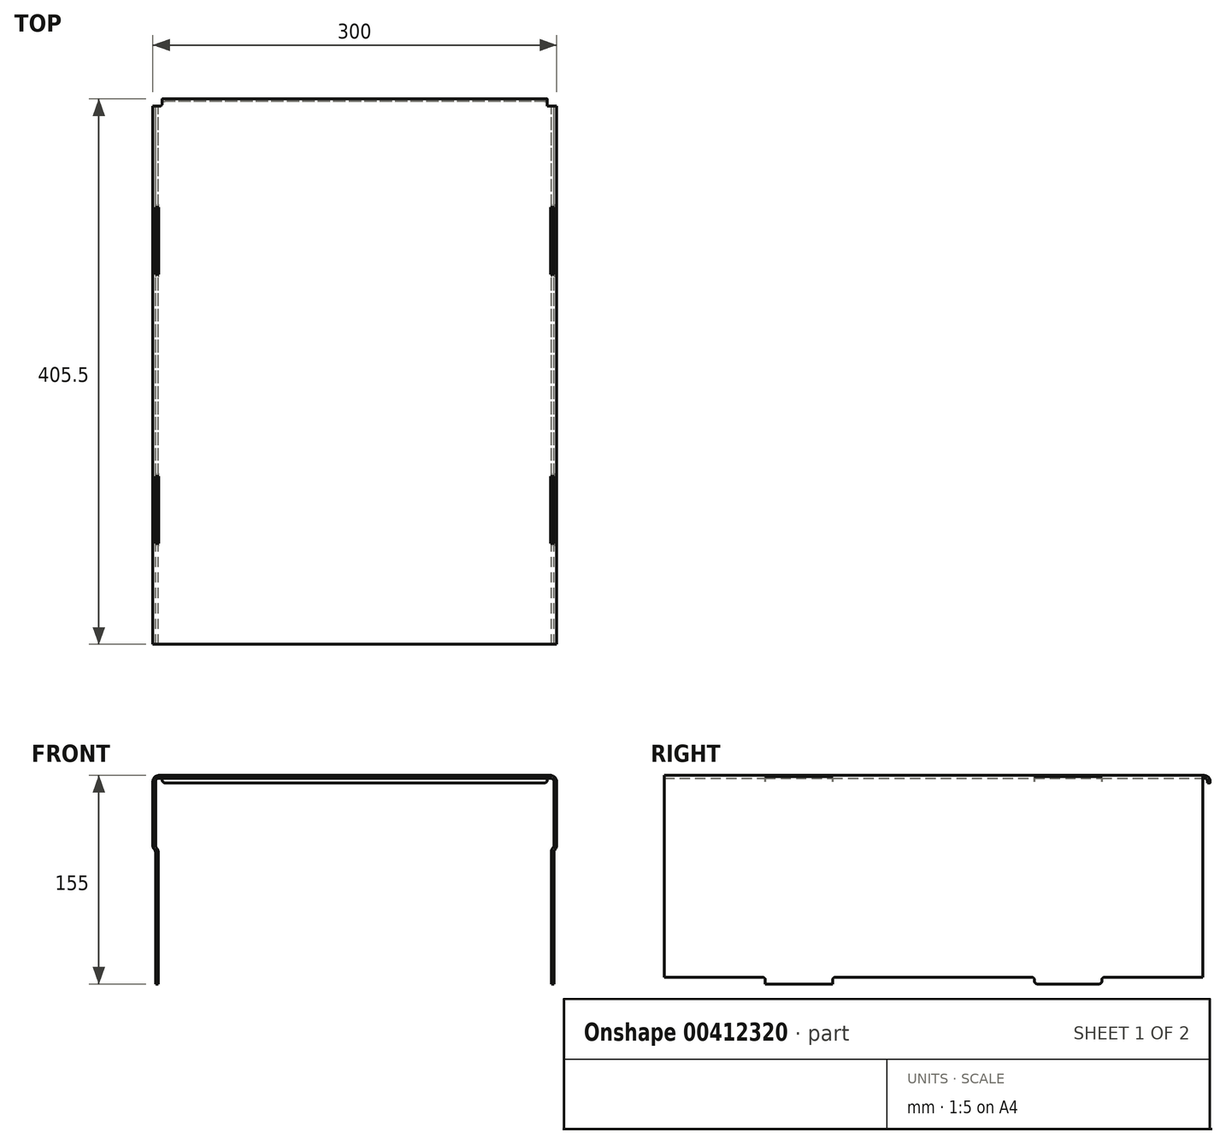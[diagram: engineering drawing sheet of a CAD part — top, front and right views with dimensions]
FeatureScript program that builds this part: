
annotation { "Feature Type Name" : "Feature", "Feature Type Description" : "" }
export const myFeature = defineFeature(function(context is Context, id is Id, definition is map)
    precondition{}
    {
        {
            var Q0;
            Q0=qCreatedBy(makeId("Front.planeOp"),FACE);
            var sketch = newSketch(context, id + "F0", { "sketchPlane" : qUnion([Q0])});
            skLineSegment(sketch, "E0.bottom", {"start": v(145.5, 77.5) * mm, "end": v(0, 77.5) * mm});
            skLineSegment(sketch, "E0.top", {"start": v(148, -77.5) * mm, "end": v(146, -77.5) * mm});
            skLineSegment(sketch, "E0.left", {"start": v(150, 73) * mm, "end": v(150, 25.5) * mm});
            skPoint(sketch, "E0.middle", {"position": v(0, 0) * mm});
            skLineSegment(sketch, "E1", {"start": v(148.95, 22.6) * mm, "end": v(148.58, 22.18) * mm});
            skLineSegment(sketch, "E2", {"start": v(148, 20.57) * mm, "end": v(148, -77.5) * mm});
            skPoint(sketch, "E3.visualSharp", {"position": v(150, 77.5) * mm});
            skArc(sketch, "E3.filletArc", {"start": v(150, 73) * mm, "mid": v(148.68, 76.18) * mm, "end": v(145.5, 77.5) * mm});
            skLineSegment(sketch, "E4", {"start": v(0, 75.5) * mm, "end": v(145.5, 75.5) * mm});
            skLineSegment(sketch, "E5.trimOffspring", {"start": v(148, 73) * mm, "end": v(148, 25.5) * mm});
            skPoint(sketch, "E6.visualSharp", {"position": v(148, 75.5) * mm});
            skArc(sketch, "E6.filletArc", {"start": v(148, 73) * mm, "mid": v(147.27, 74.77) * mm, "end": v(145.5, 75.5) * mm});
            skLineSegment(sketch, "E7", {"start": v(147.42, 23.9) * mm, "end": v(147.05, 23.46) * mm});
            skLineSegment(sketch, "E8", {"start": v(146, 20.57) * mm, "end": v(146, -77.5) * mm});
            skPoint(sketch, "E9.orphan", {"position": v(150, -77.5) * mm});
            skPoint(sketch, "E10.visualSharp", {"position": v(150, 23.86) * mm});
            skArc(sketch, "E10.filletArc", {"start": v(148.95, 22.6) * mm, "mid": v(149.73, 23.96) * mm, "end": v(150, 25.5) * mm});
            skPoint(sketch, "E11.visualSharp", {"position": v(148, 21.48) * mm});
            skArc(sketch, "E11.filletArc", {"start": v(148.58, 22.18) * mm, "mid": v(148.15, 21.42) * mm, "end": v(148, 20.57) * mm});
            skPoint(sketch, "E12.visualSharp", {"position": v(148, 24.6) * mm});
            skArc(sketch, "E12.filletArc", {"start": v(147.42, 23.9) * mm, "mid": v(147.85, 24.64) * mm, "end": v(148, 25.5) * mm});
            skPoint(sketch, "E13.visualSharp", {"position": v(146, 22.2) * mm});
            skArc(sketch, "E13.filletArc", {"start": v(147.05, 23.46) * mm, "mid": v(146.27, 22.1) * mm, "end": v(146, 20.57) * mm});
            skLineSegment(sketch, "E14", {"start": v(0, 0) * mm, "end": v(0, 158.87) * mm, "construction": true});
            skPoint(sketch, "E0.right.start.orphan", {"position": v(-150, 77.5) * mm});
            skLineSegment(sketch, "E15.MirrorCS", {"start": v(-145.5, 77.5) * mm, "end": v(0, 77.5) * mm});
            skLineSegment(sketch, "E16.MirrorCS", {"start": v(0, 75.5) * mm, "end": v(-145.5, 75.5) * mm});
            skArc(sketch, "E17.MirrorCS", {"start": v(-148, 73) * mm, "mid": v(-147.27, 74.77) * mm, "end": v(-145.5, 75.5) * mm});
            skArc(sketch, "E18.MirrorCS", {"start": v(-150, 73) * mm, "mid": v(-148.68, 76.18) * mm, "end": v(-145.5, 77.5) * mm});
            skLineSegment(sketch, "E19.MirrorCS", {"start": v(-148, 73) * mm, "end": v(-148, 25.5) * mm});
            skLineSegment(sketch, "E20.MirrorCS", {"start": v(-150, 73) * mm, "end": v(-150, 25.5) * mm});
            skLineSegment(sketch, "E21.MirrorCS", {"start": v(-148, 20.57) * mm, "end": v(-148, -77.5) * mm});
            skLineSegment(sketch, "E22.MirrorCS", {"start": v(-146, 20.57) * mm, "end": v(-146, -77.5) * mm});
            skArc(sketch, "E23.MirrorCS", {"start": v(-147.05, 23.46) * mm, "mid": v(-146.27, 22.1) * mm, "end": v(-146, 20.57) * mm});
            skArc(sketch, "E24.MirrorCS", {"start": v(-148.58, 22.18) * mm, "mid": v(-148.15, 21.42) * mm, "end": v(-148, 20.57) * mm});
            skArc(sketch, "E25.MirrorCS", {"start": v(-147.42, 23.9) * mm, "mid": v(-147.85, 24.64) * mm, "end": v(-148, 25.5) * mm});
            skArc(sketch, "E26.MirrorCS", {"start": v(-148.95, 22.6) * mm, "mid": v(-149.73, 23.96) * mm, "end": v(-150, 25.5) * mm});
            skLineSegment(sketch, "E27", {"start": v(-147.42, 23.9) * mm, "end": v(-147.05, 23.46) * mm});
            skLineSegment(sketch, "E28", {"start": v(-148.95, 22.6) * mm, "end": v(-148.58, 22.18) * mm});
            skLineSegment(sketch, "E29.trimOffspring", {"start": v(-146, -77.5) * mm, "end": v(-150, -77.5) * mm});
            skSolve(sketch);
        }
        {
            var Q0;
            Q0 = qSketchRegion(id + "F0", true);
            extrude(context, id + "F1", {"entities" : qUnion([Q0]), "depth" : 400 * mm});
        }
        {
            var Q0;
            Q0=makeQuery(id+"F1.opExtrude","SWEPT_FACE",FACE,{"disambiguationData":[OSD([sQuery(id+"F0.wireOp",EDGE,"E2")])]});
            var sketch = newSketch(context, id + "F2", { "sketchPlane" : qUnion([Q0])});
            skLineSegment(sketch, "E30", {"start": v(-430.94, -72.5) * mm, "end": v(45.78, -72.5) * mm});
            skLineSegment(sketch, "E31.bottom", {"start": v(-400, -77.5) * mm, "end": v(-325, -77.5) * mm});
            skLineSegment(sketch, "E31.top", {"start": v(-400, -72.5) * mm, "end": v(-325, -72.5) * mm});
            skLineSegment(sketch, "E31.left", {"start": v(-400, -77.5) * mm, "end": v(-400, -72.5) * mm});
            skLineSegment(sketch, "E31.right", {"start": v(-325, -77.5) * mm, "end": v(-325, -72.5) * mm});
            skLineSegment(sketch, "E32.bottom", {"start": v(0, -77.5) * mm, "end": v(-75, -77.5) * mm});
            skLineSegment(sketch, "E32.top", {"start": v(0, -72.5) * mm, "end": v(-75, -72.5) * mm});
            skLineSegment(sketch, "E32.left", {"start": v(0, -77.5) * mm, "end": v(0, -72.5) * mm});
            skLineSegment(sketch, "E32.right", {"start": v(-75, -77.5) * mm, "end": v(-75, -72.5) * mm});
            skLineSegment(sketch, "E33", {"start": v(-200, 111) * mm, "end": v(-200, -165.3) * mm, "construction": true});
            skPoint(sketch, "E33.startSnap0", {"position": v(-200, 20.57) * mm});
            skLineSegment(sketch, "E34.bottom", {"start": v(-125, -72.5) * mm, "end": v(-275, -72.5) * mm, "construction": true});
            skLineSegment(sketch, "E34.top", {"start": v(-125, -129.42) * mm, "end": v(-275, -129.42) * mm, "construction": true});
            skLineSegment(sketch, "E34.left", {"start": v(-125, -72.5) * mm, "end": v(-125, -129.42) * mm});
            skLineSegment(sketch, "E34.right", {"start": v(-275, -72.5) * mm, "end": v(-275, -129.42) * mm});
            skPoint(sketch, "E34.middle", {"position": v(-200, -100.96) * mm});
            skSolve(sketch);
        }
        {
            var Q0;
            {var subQ0=sQuery(id+"F2.wireOp",EDGE,"E34.left");var subQ1=sQuery(id+"F2.wireOp",EDGE,"E30");var subQ2=makeQuery(id+"F2.imprint","INTERSECT",VERTEX,{"derivedFrom":[subQ1,subQ0]});Q0=makeQuery(id+"F2.imprint","IMPRINT",FACE,{"disambiguationData":[TD([[makeQuery(id+"F2.imprint","IMPRINT",EDGE,{"disambiguationData":[TD([[subQ2,1.0]])],"derivedFrom":subQ1}),-1.0]])]});}
            var Q1;
            Q1=makeQuery(id+"F2.imprint","IMPRINT",FACE,{"disambiguationData":[TD([[makeQuery(id+"F2.imprint","IMPRINT",EDGE,{"derivedFrom":sQuery(id+"F2.wireOp",EDGE,"E32.bottom")}),1.0]])]});
            var Q2;
            Q2=makeQuery(id+"F2.imprint","IMPRINT",FACE,{"disambiguationData":[TD([[makeQuery(id+"F2.imprint","IMPRINT",EDGE,{"derivedFrom":sQuery(id+"F2.wireOp",EDGE,"E31.bottom")}),1.0]])]});
            extrude(context, id + "F3", {"entities" : qUnion([Q0, Q1, Q2]), "operationType" : NewBodyOperationType.REMOVE, "oppositeDirection" : true, "depth" : 645 * mm});
        }
        {
            var Q0;
            Q0=makeQuery(id+"F1.opExtrude","SWEPT_FACE",FACE,{"disambiguationData":[OSD([sQuery(id+"F0.wireOp",EDGE,"E0.bottom"),sQuery(id+"F0.wireOp",EDGE,"E15.MirrorCS")])]});
            var sketch = newSketch(context, id + "F4", { "sketchPlane" : qUnion([Q0])});
            skLineSegment(sketch, "E35", {"start": v(-145.5, -200) * mm, "end": v(196.76, -200) * mm, "construction": true});
            skLineSegment(sketch, "E36", {"start": v(0, 0) * mm, "end": v(0, -263.53) * mm, "construction": true});
            skLineSegment(sketch, "E37.bottom", {"start": v(148, -125) * mm, "end": v(145.5, -125) * mm});
            skLineSegment(sketch, "E37.top", {"start": v(148, -75) * mm, "end": v(145.5, -75) * mm});
            skLineSegment(sketch, "E37.left", {"start": v(148, -125) * mm, "end": v(148, -75) * mm});
            skLineSegment(sketch, "E37.right", {"start": v(145.5, -125) * mm, "end": v(145.5, -75) * mm});
            skPoint(sketch, "E37.middle", {"position": v(146.75, -100) * mm});
            skLineSegment(sketch, "E38.MirrorCS", {"start": v(148, -325) * mm, "end": v(145.5, -325) * mm});
            skLineSegment(sketch, "E39.MirrorCS", {"start": v(145.5, -275) * mm, "end": v(145.5, -325) * mm});
            skLineSegment(sketch, "E40.MirrorCS", {"start": v(148, -275) * mm, "end": v(148, -325) * mm});
            skLineSegment(sketch, "E41.MirrorCS", {"start": v(148, -275) * mm, "end": v(145.5, -275) * mm});
            skLineSegment(sketch, "E42.MirrorCS", {"start": v(-148, -75) * mm, "end": v(-145.5, -75) * mm});
            skLineSegment(sketch, "E43.MirrorCS", {"start": v(-148, -125) * mm, "end": v(-145.5, -125) * mm});
            skLineSegment(sketch, "E44.MirrorCS", {"start": v(-145.5, -125) * mm, "end": v(-145.5, -75) * mm});
            skLineSegment(sketch, "E45.MirrorCS", {"start": v(-148, -125) * mm, "end": v(-148, -75) * mm});
            skPoint(sketch, "E46.MirrorP", {"position": v(-146.75, -100) * mm});
            skLineSegment(sketch, "E47.MirrorCS", {"start": v(-148, -325) * mm, "end": v(-145.5, -325) * mm});
            skLineSegment(sketch, "E48.MirrorCS", {"start": v(-148, -275) * mm, "end": v(-145.5, -275) * mm});
            skLineSegment(sketch, "E49.MirrorCS", {"start": v(-145.5, -275) * mm, "end": v(-145.5, -325) * mm});
            skLineSegment(sketch, "E50.MirrorCS", {"start": v(-148, -275) * mm, "end": v(-148, -325) * mm});
            skSolve(sketch);
        }
        {
            var Q0;
            Q0=makeQuery(id+"F4.imprint","IMPRINT",FACE,{"disambiguationData":[TD([[makeQuery(id+"F4.imprint","IMPRINT",EDGE,{"derivedFrom":sQuery(id+"F4.wireOp",EDGE,"E37.bottom")}),-1.0]])]});
            var Q1;
            Q1=makeQuery(id+"F4.imprint","IMPRINT",FACE,{"disambiguationData":[TD([[makeQuery(id+"F4.imprint","IMPRINT",EDGE,{"derivedFrom":sQuery(id+"F4.wireOp",EDGE,"E38.MirrorCS")}),-1.0]])]});
            var Q2;
            Q2=makeQuery(id+"F4.imprint","IMPRINT",FACE,{"disambiguationData":[TD([[makeQuery(id+"F4.imprint","IMPRINT",EDGE,{"derivedFrom":sQuery(id+"F4.wireOp",EDGE,"E42.MirrorCS")}),-1.0]])]});
            var Q3;
            Q3=makeQuery(id+"F4.imprint","IMPRINT",FACE,{"disambiguationData":[TD([[makeQuery(id+"F4.imprint","IMPRINT",EDGE,{"derivedFrom":sQuery(id+"F4.wireOp",EDGE,"E47.MirrorCS")}),1.0]])]});
            var Q4;
            Q4=sQuery(id+"F4.wireOp",EDGE,"E35");
            var Q5;
            Q5=sQuery(id+"F4.wireOp",EDGE,"E36");
            extrude(context, id + "F5", {"entities" : qUnion([Q0, Q1, Q2, Q3]), "operationType" : NewBodyOperationType.REMOVE, "surfaceEntities" : qUnion([Q4, Q5]), "oppositeDirection" : true, "depth" : 21 * mm});
        }
        {
            var Q0;
            {var subQ0=sQuery(id+"F2.wireOp",EDGE,"E30");var subQ1=sQuery(id+"F2.wireOp",EDGE,"E34.left");Q0=makeQuery(id+"F3.boolean.opBoolean","COPY",EDGE,{"disambiguationData":[TD([makeQuery(id+"F1.opExtrude","SWEPT_FACE",FACE,{"disambiguationData":[OSD([sQuery(id+"F0.wireOp",EDGE,"E2")])]})])],"derivedFrom":makeQuery(id+"F3.opExtrude","SWEPT_EDGE",EDGE,{"disambiguationData":[OSD([subQ0,subQ1])]})});}
            var Q1;
            {var subQ0=sQuery(id+"F2.wireOp",EDGE,"E31.right");var subQ1=sQuery(id+"F2.wireOp",EDGE,"E31.top");Q1=makeQuery(id+"F3.boolean.opBoolean","COPY",EDGE,{"disambiguationData":[TD([makeQuery(id+"F1.opExtrude","SWEPT_FACE",FACE,{"disambiguationData":[OSD([sQuery(id+"F0.wireOp",EDGE,"E2")])]})])],"derivedFrom":makeQuery(id+"F3.opExtrude","SWEPT_EDGE",EDGE,{"disambiguationData":[OSD([sQuery(id+"F2.wireOp",EDGE,"E30"),subQ1,subQ0])]})});}
            var Q2;
            {var subQ0=sQuery(id+"F2.wireOp",EDGE,"E31.right");var subQ1=sQuery(id+"F2.wireOp",EDGE,"E31.top");Q2=makeQuery(id+"F3.boolean.opBoolean","COPY",EDGE,{"disambiguationData":[TD([makeQuery(id+"F1.opExtrude","SWEPT_FACE",FACE,{"disambiguationData":[OSD([sQuery(id+"F0.wireOp",EDGE,"E21.MirrorCS")])]})])],"derivedFrom":makeQuery(id+"F3.opExtrude","SWEPT_EDGE",EDGE,{"disambiguationData":[OSD([sQuery(id+"F2.wireOp",EDGE,"E30"),subQ1,subQ0])]})});}
            var Q3;
            {var subQ0=sQuery(id+"F2.wireOp",EDGE,"E30");var subQ1=sQuery(id+"F2.wireOp",EDGE,"E34.left");Q3=makeQuery(id+"F3.boolean.opBoolean","COPY",EDGE,{"disambiguationData":[TD([makeQuery(id+"F1.opExtrude","SWEPT_FACE",FACE,{"disambiguationData":[OSD([sQuery(id+"F0.wireOp",EDGE,"E21.MirrorCS")])]})])],"derivedFrom":makeQuery(id+"F3.opExtrude","SWEPT_EDGE",EDGE,{"disambiguationData":[OSD([subQ0,subQ1])]})});}
            var Q4;
            {var subQ0=sQuery(id+"F2.wireOp",EDGE,"E32.right");var subQ1=sQuery(id+"F2.wireOp",EDGE,"E32.top");Q4=makeQuery(id+"F3.boolean.opBoolean","COPY",EDGE,{"disambiguationData":[TD([makeQuery(id+"F1.opExtrude","SWEPT_FACE",FACE,{"disambiguationData":[OSD([sQuery(id+"F0.wireOp",EDGE,"E2")])]})])],"derivedFrom":makeQuery(id+"F3.opExtrude","SWEPT_EDGE",EDGE,{"disambiguationData":[OSD([sQuery(id+"F2.wireOp",EDGE,"E30"),subQ1,subQ0])]})});}
            var Q5;
            {var subQ0=sQuery(id+"F2.wireOp",EDGE,"E30");var subQ1=sQuery(id+"F2.wireOp",EDGE,"E34.right");Q5=makeQuery(id+"F3.boolean.opBoolean","COPY",EDGE,{"disambiguationData":[TD([makeQuery(id+"F1.opExtrude","SWEPT_FACE",FACE,{"disambiguationData":[OSD([sQuery(id+"F0.wireOp",EDGE,"E2")])]})])],"derivedFrom":makeQuery(id+"F3.opExtrude","SWEPT_EDGE",EDGE,{"disambiguationData":[OSD([subQ0,subQ1])]})});}
            var Q6;
            {var subQ0=sQuery(id+"F2.wireOp",EDGE,"E30");var subQ1=sQuery(id+"F2.wireOp",EDGE,"E34.right");Q6=makeQuery(id+"F3.boolean.opBoolean","COPY",EDGE,{"disambiguationData":[TD([makeQuery(id+"F1.opExtrude","SWEPT_FACE",FACE,{"disambiguationData":[OSD([sQuery(id+"F0.wireOp",EDGE,"E21.MirrorCS")])]})])],"derivedFrom":makeQuery(id+"F3.opExtrude","SWEPT_EDGE",EDGE,{"disambiguationData":[OSD([subQ0,subQ1])]})});}
            var Q7;
            {var subQ0=sQuery(id+"F2.wireOp",EDGE,"E32.right");var subQ1=sQuery(id+"F2.wireOp",EDGE,"E32.top");Q7=makeQuery(id+"F3.boolean.opBoolean","COPY",EDGE,{"disambiguationData":[TD([makeQuery(id+"F1.opExtrude","SWEPT_FACE",FACE,{"disambiguationData":[OSD([sQuery(id+"F0.wireOp",EDGE,"E21.MirrorCS")])]})])],"derivedFrom":makeQuery(id+"F3.opExtrude","SWEPT_EDGE",EDGE,{"disambiguationData":[OSD([sQuery(id+"F2.wireOp",EDGE,"E30"),subQ1,subQ0])]})});}
            var Q8;
            {var subQ0=sQuery(id+"F0.wireOp",EDGE,"E0.top");var subQ1=sQuery(id+"F2.wireOp",EDGE,"E31.right");Q8=makeQuery(id+"F3.boolean.opBoolean","COPY",EDGE,{"disambiguationData":[topologyDisambiguationEdgeConnected([makeQuery(id+"F1.opExtrude","SWEPT_FACE",FACE,{"disambiguationData":[OSD([subQ0])]})])],"derivedFrom":makeQuery(id+"F3.opExtrude","SWEPT_EDGE",EDGE,{"disambiguationData":[OSD([subQ0,sQuery(id+"F0.wireOp",EDGE,"E2"),sQuery(id+"F2.wireOp",EDGE,"E31.bottom"),subQ1])]})});}
            var Q9;
            {var subQ0=sQuery(id+"F0.wireOp",EDGE,"E0.top");var subQ1=sQuery(id+"F2.wireOp",EDGE,"E34.left");Q9=makeQuery(id+"F3.boolean.opBoolean","COPY",EDGE,{"disambiguationData":[topologyDisambiguationEdgeConnected([makeQuery(id+"F1.opExtrude","SWEPT_FACE",FACE,{"disambiguationData":[OSD([subQ0])]})])],"derivedFrom":makeQuery(id+"F3.opExtrude","SWEPT_EDGE",EDGE,{"disambiguationData":[OSD([subQ0,sQuery(id+"F0.wireOp",EDGE,"E2"),subQ1])]})});}
            var Q10;
            {var subQ0=sQuery(id+"F2.wireOp",EDGE,"E31.right");Q10=makeQuery(id+"F3.boolean.opBoolean","COPY",EDGE,{"disambiguationData":[topologyDisambiguationEdgeConnected([makeQuery(id+"F1.opExtrude","SWEPT_FACE",FACE,{"disambiguationData":[OSD([sQuery(id+"F0.wireOp",EDGE,"E29.trimOffspring")])]})])],"derivedFrom":makeQuery(id+"F3.opExtrude","SWEPT_EDGE",EDGE,{"disambiguationData":[OSD([sQuery(id+"F0.wireOp",EDGE,"E0.top"),sQuery(id+"F0.wireOp",EDGE,"E2"),sQuery(id+"F2.wireOp",EDGE,"E31.bottom"),subQ0])]})});}
            var Q11;
            {var subQ0=sQuery(id+"F2.wireOp",EDGE,"E34.left");Q11=makeQuery(id+"F3.boolean.opBoolean","COPY",EDGE,{"disambiguationData":[topologyDisambiguationEdgeConnected([makeQuery(id+"F1.opExtrude","SWEPT_FACE",FACE,{"disambiguationData":[OSD([sQuery(id+"F0.wireOp",EDGE,"E29.trimOffspring")])]})])],"derivedFrom":makeQuery(id+"F3.opExtrude","SWEPT_EDGE",EDGE,{"disambiguationData":[OSD([sQuery(id+"F0.wireOp",EDGE,"E0.top"),sQuery(id+"F0.wireOp",EDGE,"E2"),subQ0])]})});}
            var Q12;
            {var subQ0=sQuery(id+"F0.wireOp",EDGE,"E0.top");var subQ1=sQuery(id+"F2.wireOp",EDGE,"E34.right");Q12=makeQuery(id+"F3.boolean.opBoolean","COPY",EDGE,{"disambiguationData":[topologyDisambiguationEdgeConnected([makeQuery(id+"F1.opExtrude","SWEPT_FACE",FACE,{"disambiguationData":[OSD([subQ0])]})])],"derivedFrom":makeQuery(id+"F3.opExtrude","SWEPT_EDGE",EDGE,{"disambiguationData":[OSD([subQ0,sQuery(id+"F0.wireOp",EDGE,"E2"),subQ1])]})});}
            var Q13;
            {var subQ0=sQuery(id+"F0.wireOp",EDGE,"E0.top");var subQ1=sQuery(id+"F2.wireOp",EDGE,"E32.right");Q13=makeQuery(id+"F3.boolean.opBoolean","COPY",EDGE,{"disambiguationData":[topologyDisambiguationEdgeConnected([makeQuery(id+"F1.opExtrude","SWEPT_FACE",FACE,{"disambiguationData":[OSD([subQ0])]})])],"derivedFrom":makeQuery(id+"F3.opExtrude","SWEPT_EDGE",EDGE,{"disambiguationData":[OSD([subQ0,sQuery(id+"F0.wireOp",EDGE,"E2"),sQuery(id+"F2.wireOp",EDGE,"E32.bottom"),subQ1])]})});}
            var Q14;
            {var subQ0=sQuery(id+"F2.wireOp",EDGE,"E34.right");Q14=makeQuery(id+"F3.boolean.opBoolean","COPY",EDGE,{"disambiguationData":[topologyDisambiguationEdgeConnected([makeQuery(id+"F1.opExtrude","SWEPT_FACE",FACE,{"disambiguationData":[OSD([sQuery(id+"F0.wireOp",EDGE,"E29.trimOffspring")])]})])],"derivedFrom":makeQuery(id+"F3.opExtrude","SWEPT_EDGE",EDGE,{"disambiguationData":[OSD([sQuery(id+"F0.wireOp",EDGE,"E0.top"),sQuery(id+"F0.wireOp",EDGE,"E2"),subQ0])]})});}
            var Q15;
            {var subQ0=sQuery(id+"F2.wireOp",EDGE,"E32.right");Q15=makeQuery(id+"F3.boolean.opBoolean","COPY",EDGE,{"disambiguationData":[topologyDisambiguationEdgeConnected([makeQuery(id+"F1.opExtrude","SWEPT_FACE",FACE,{"disambiguationData":[OSD([sQuery(id+"F0.wireOp",EDGE,"E29.trimOffspring")])]})])],"derivedFrom":makeQuery(id+"F3.opExtrude","SWEPT_EDGE",EDGE,{"disambiguationData":[OSD([sQuery(id+"F0.wireOp",EDGE,"E0.top"),sQuery(id+"F0.wireOp",EDGE,"E2"),sQuery(id+"F2.wireOp",EDGE,"E32.bottom"),subQ0])]})});}
            fillet(context, id + "F6", {"entities" : qUnion([Q0, Q1, Q2, Q3, Q4, Q5, Q6, Q7, Q8, Q9, Q10, Q11, Q12, Q13, Q14, Q15]), "radius" : 2 * mm, "tangentPropagation" : true, "allowEdgeOverflow" : false});
        }
        {
            var Q0;
            Q0=qCreatedBy(makeId("Right.planeOp"),FACE);
            var sketch = newSketch(context, id + "F7", { "sketchPlane" : qUnion([Q0])});
            skLineSegment(sketch, "E51", {"start": v(0, 77.5) * mm, "end": v(1, 77.5) * mm});
            skLineSegment(sketch, "E52", {"start": v(5.5, 73) * mm, "end": v(5.5, 72) * mm});
            skLineSegment(sketch, "E53", {"start": v(5.5, 72) * mm, "end": v(3.5, 72) * mm});
            skLineSegment(sketch, "E54", {"start": v(3.5, 72) * mm, "end": v(3.5, 73) * mm});
            skLineSegment(sketch, "E55", {"start": v(1, 75.5) * mm, "end": v(0, 75.5) * mm});
            skLineSegment(sketch, "E56", {"start": v(0, 75.5) * mm, "end": v(0, 77.5) * mm});
            skPoint(sketch, "E57.visualSharp", {"position": v(5.5, 77.5) * mm});
            skArc(sketch, "E57.filletArc", {"start": v(5.5, 73) * mm, "mid": v(4.18, 76.18) * mm, "end": v(1, 77.5) * mm});
            skPoint(sketch, "E58.visualSharp", {"position": v(3.5, 75.5) * mm});
            skArc(sketch, "E58.filletArc", {"start": v(3.5, 73) * mm, "mid": v(2.77, 74.77) * mm, "end": v(1, 75.5) * mm});
            skSolve(sketch);
        }
        {
            var Q0;
            Q0=makeQuery(id+"F7.imprint","IMPRINT",FACE,{"disambiguationData":[TD([[makeQuery(id+"F7.imprint","IMPRINT",EDGE,{"derivedFrom":sQuery(id+"F7.wireOp",EDGE,"E51")}),-1.0]])]});
            var Q1;
            Q1=makeQuery(id+"F1.opExtrude","CAP_VERTEX",VERTEX,{"disambiguationData":[OSD([sQuery(id+"F0.wireOp",EDGE,"E0.bottom"),sQuery(id+"F0.wireOp",EDGE,"E3.filletArc")])],"isStart":true});
            var Q2;
            Q2=sQuery(id+"F7.wireOp",VERTEX,"E58.filletArc.end");
            extrude(context, id + "F8", {"entities" : qUnion([Q0]), "operationType" : NewBodyOperationType.ADD, "endBoundEntityVertex" : qUnion([Q1]), "depth" : 143 * mm, "hasSecondDirection" : true, "secondDirectionOppositeDirection" : true, "secondDirectionBoundEntityVertex" : qUnion([Q2]), "secondDirectionDepth" : 143 * mm});
        }
        {
            var Q0;
            Q0=makeQuery(id+"F8.opExtrude","CAP_EDGE",EDGE,{"disambiguationData":[OSD([sQuery(id+"F7.wireOp",EDGE,"E56")])],"isStart":false});
            var Q1;
            Q1=makeQuery(id+"F8.opExtrude","CAP_EDGE",EDGE,{"disambiguationData":[OSD([sQuery(id+"F7.wireOp",EDGE,"E56")])],"isStart":true});
            var Q2;
            Q2=makeQuery(id+"F8.opExtrude","CAP_EDGE",EDGE,{"disambiguationData":[OSD([sQuery(id+"F7.wireOp",EDGE,"E53")])],"isStart":true});
            var Q3;
            Q3=makeQuery(id+"F8.opExtrude","CAP_EDGE",EDGE,{"disambiguationData":[OSD([sQuery(id+"F7.wireOp",EDGE,"E53")])],"isStart":false});
            fillet(context, id + "F9", {"entities" : qUnion([Q0, Q1, Q2, Q3]), "radius" : 2 * mm, "tangentPropagation" : true, "allowEdgeOverflow" : false});
        }
    });
